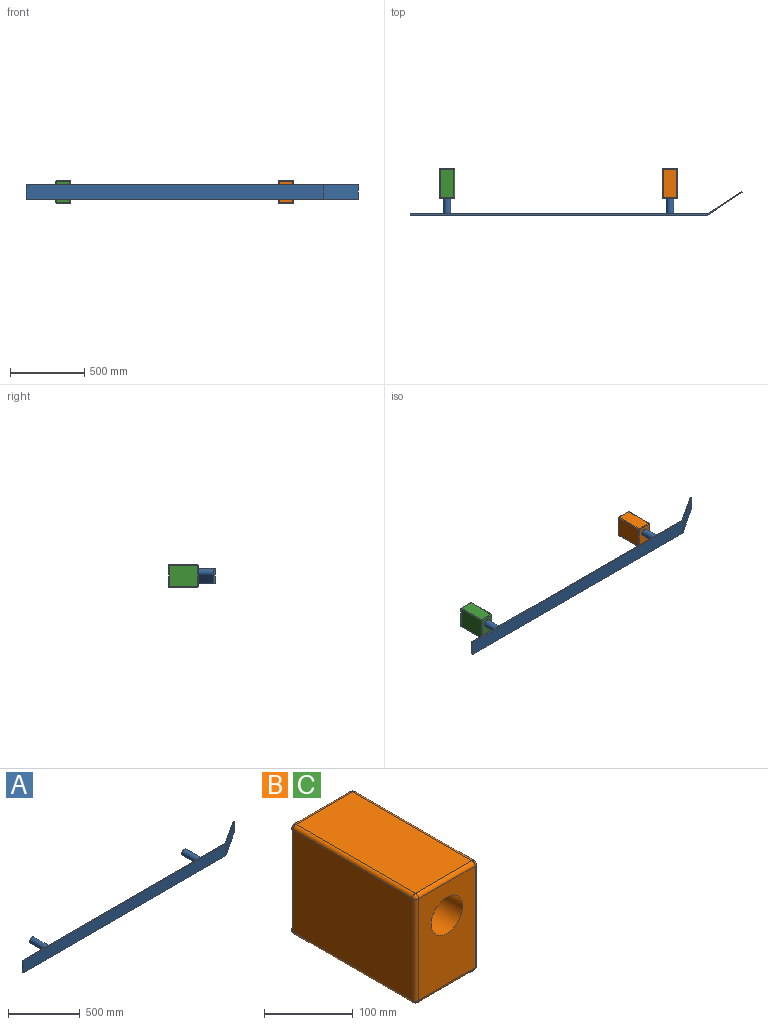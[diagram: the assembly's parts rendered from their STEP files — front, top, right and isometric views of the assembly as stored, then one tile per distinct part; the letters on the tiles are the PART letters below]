
ASSEMBLY  parts=3 mates=3
PART A: 12 faces, bbox 2234.1x160x100 mm
  f0: plane 2234.13x160mm, normal (0,0,-1), area 21996.6mm2, adj f1,f3,f4,f9,f10,f11
  f1: plane 2000x100mm, normal (0,1,0), area 196073mm2, adj f0,f2,f4,f5,f7,f9
  f2: plane 2234.13x160mm, normal (0,0,1), area 21996.6mm2, adj f1,f3,f4,f9,f10,f11
  f3: plane 2000x100mm, normal (0,-1,0), area 200000mm2, adj f0,f2,f4,f10
  f4: plane 100x10mm, normal (-1,0,0), area 1000mm2, adj f0,f1,f2,f3
  f5: cylinder r=25mm len=150mm, axis (0,-1,0), area 23561.9mm2, adj f1,f6
  f6: plane 50x50mm, normal (0,1,0), area 1963.5mm2, adj f5
  f7: cylinder r=25mm len=150mm, axis (0,-1,0), area 23561.9mm2, adj f1,f8
  f8: plane 50x50mm, normal (0,1,0), area 1963.5mm2, adj f7
  f9: plane 230.86x150mm, normal (-0.54,0.84,0), area 27531.3mm2, adj f0,f1,f2,f11
  f10: plane 234.13x154.97mm, normal (0.55,-0.83,0), area 28077.1mm2, adj f0,f2,f3,f11
  f11: plane 100x5.03mm, normal (0.84,0.54,0), area 600mm2, adj f0,f2,f9,f10
PART B: 28 faces, bbox 100x200x150 mm
  f0: plane 190x90mm, normal (0,0,1), area 17100mm2, adj f16,f21,f24,f27
  f1: plane 190x140mm, normal (-1,0,0), area 26600mm2, adj f13,f22,f23,f27
  f2: plane 190x90mm, normal (0,0,-1), area 17100mm2, adj f8,f12,f13,f14
  f3: plane 190x140mm, normal (1,0,0), area 26600mm2, adj f8,f11,f15,f16
  f4: plane 140x90mm, normal (0,-1,0), area 10636.5mm2, adj f6,f11,f12,f21,f22
  f5: plane 140x90mm, normal (0,1,0), area 12600mm2, adj f14,f15,f23,f24
  f6: cylinder r=25mm len=150mm, axis (0,-1,0), area 23561.9mm2, adj f4,f7
  f7: plane 50x50mm, normal (0,-1,0), area 1963.5mm2, adj f6
  f8: cylinder r=5mm len=190mm, axis (0,1,0), area 1492.3mm2, adj f2,f3,f9,f10
  f9: sphere r=5mm, area 39.3mm2, adj f8,f11,f12
  f10: sphere r=5mm, area 39.3mm2, adj f8,f14,f15
  f11: cylinder r=5mm len=140mm, axis (0,0,-1), area 1099.6mm2, adj f3,f4,f9,f17
  f12: cylinder r=5mm len=90mm, axis (-1,0,0), area 706.9mm2, adj f2,f4,f9,f18
  f13: cylinder r=5mm len=190mm, axis (0,-1,0), area 1492.3mm2, adj f1,f2,f18,f19
  f14: cylinder r=5mm len=90mm, axis (1,0,0), area 706.9mm2, adj f2,f5,f10,f19
  f15: cylinder r=5mm len=140mm, axis (0,0,1), area 1099.6mm2, adj f3,f5,f10,f20
  f16: cylinder r=5mm len=190mm, axis (0,-1,0), area 1492.3mm2, adj f0,f3,f17,f20
  f17: sphere r=5mm, area 39.3mm2, adj f11,f16,f21
  f18: sphere r=5mm, area 39.3mm2, adj f12,f13,f22
  f19: sphere r=5mm, area 39.3mm2, adj f13,f14,f23
  f20: sphere r=5mm, area 39.3mm2, adj f15,f16,f24
  f21: cylinder r=5mm len=90mm, axis (1,0,0), area 706.9mm2, adj f0,f4,f17,f25
  f22: cylinder r=5mm len=140mm, axis (0,0,1), area 1099.6mm2, adj f1,f4,f18,f25
  f23: cylinder r=5mm len=140mm, axis (0,0,-1), area 1099.6mm2, adj f1,f5,f19,f26
  f24: cylinder r=5mm len=90mm, axis (-1,0,0), area 706.9mm2, adj f0,f5,f20,f26
  f25: sphere r=5mm, area 39.3mm2, adj f21,f22,f27
  f26: sphere r=5mm, area 39.3mm2, adj f23,f24,f27
  f27: cylinder r=5mm len=190mm, axis (0,1,0), area 1492.3mm2, adj f0,f1,f25,f26
PART C: same geometry as B
PLACE A t=(-1145.7,432.95,-70.75)mm
PLACE B t=(546.65,737.95,-95.75)mm fixed
PLACE C t=(-953.35,737.95,-95.75)mm
MATE planar C.f5 <-> B.f5  axis (0,1,0) through (-895.7,737.95,-20.75)mm
MATE cylindrical A.f7 <-> C.f6  axis (0,1,0) through (-895.7,432.95,4.25)mm
MATE cylindrical A.f5 <-> B.f6  axis (0,-1,0) through (604.3,432.95,4.25)mm
